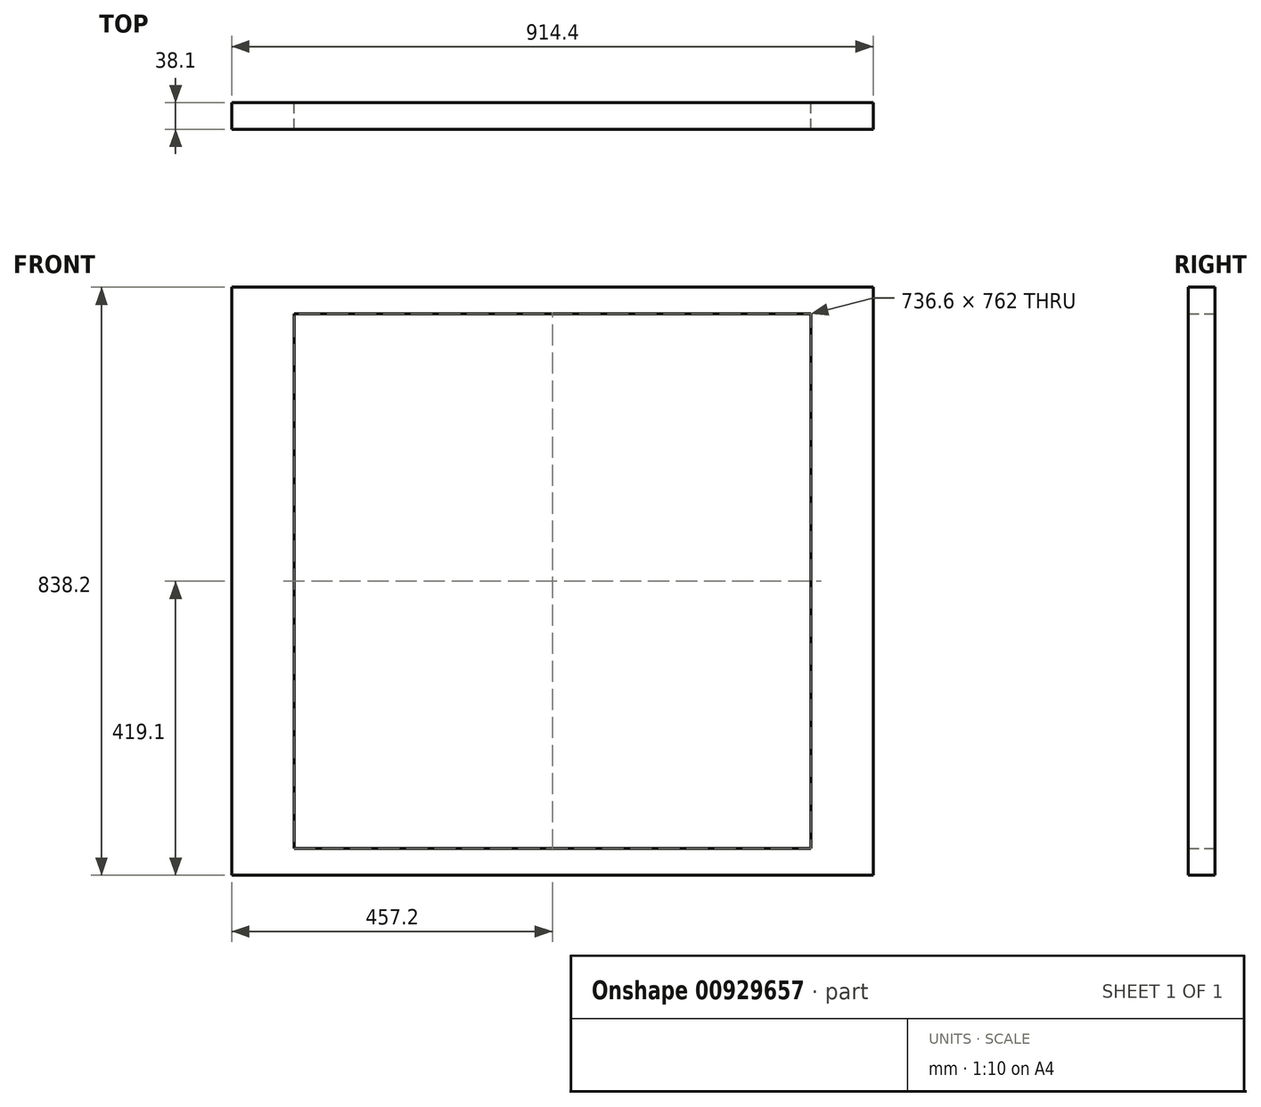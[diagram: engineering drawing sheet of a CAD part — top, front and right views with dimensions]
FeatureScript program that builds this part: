
annotation { "Feature Type Name" : "Feature", "Feature Type Description" : "" }
export const myFeature = defineFeature(function(context is Context, id is Id, definition is map)
    precondition{}
    {
        {
            var Q0;
            Q0=qCreatedBy(makeId("Front.planeOp"),FACE);
            var sketch = newSketch(context, id + "F0", { "sketchPlane" : qUnion([Q0])});
            skLineSegment(sketch, "E0.bottom", {"start": v(-44.45, -381) * mm, "end": v(44.45, -381) * mm});
            skLineSegment(sketch, "E0.top", {"start": v(-44.45, 381) * mm, "end": v(44.45, 381) * mm});
            skLineSegment(sketch, "E0.left", {"start": v(-44.45, -381) * mm, "end": v(-44.45, 381) * mm});
            skLineSegment(sketch, "E0.right", {"start": v(44.45, -381) * mm, "end": v(44.45, 381) * mm});
            skPoint(sketch, "E0.middle", {"position": v(0, 0) * mm});
            skSolve(sketch);
        }
        {
            var Q0;
            Q0 = qSketchRegion(id + "F0", true);
            extrude(context, id + "F1", {"entities" : qUnion([Q0]), "depth" : 38.1 * mm, "offsetDistance" : 25.4 * mm});
        }
        {
            var Q0;
            Q0=qCreatedBy(makeId("Front.planeOp"),FACE);
            var sketch = newSketch(context, id + "F2", { "sketchPlane" : qUnion([Q0])});
            skLineSegment(sketch, "E1.bottom", {"start": v(-44.45, 381) * mm, "end": v(869.95, 381) * mm});
            skLineSegment(sketch, "E1.top", {"start": v(-44.45, 419.1) * mm, "end": v(869.95, 419.1) * mm});
            skLineSegment(sketch, "E1.left", {"start": v(-44.45, 381) * mm, "end": v(-44.45, 419.1) * mm});
            skLineSegment(sketch, "E1.right", {"start": v(869.95, 381) * mm, "end": v(869.95, 419.1) * mm});
            skSolve(sketch);
        }
        {
            var Q0;
            Q0=makeQuery(id+"F2.imprint","IMPRINT",FACE,{"disambiguationData":[TD([[makeQuery(id+"F2.imprint","IMPRINT",EDGE,{"derivedFrom":sQuery(id+"F2.wireOp",EDGE,"E1.bottom")}),1.0]])]});
            extrude(context, id + "F3", {"entities" : qUnion([Q0]), "operationType" : NewBodyOperationType.ADD, "depth" : 38.1 * mm, "offsetDistance" : 25.4 * mm});
        }
        {
            var Q0;
            Q0=qCreatedBy(makeId("Front.planeOp"),FACE);
            var sketch = newSketch(context, id + "F4", { "sketchPlane" : qUnion([Q0])});
            skLineSegment(sketch, "E2.bottom", {"start": v(781.05, -381) * mm, "end": v(869.95, -381) * mm});
            skLineSegment(sketch, "E2.top", {"start": v(781.05, 381) * mm, "end": v(869.95, 381) * mm});
            skLineSegment(sketch, "E2.left", {"start": v(781.05, -381) * mm, "end": v(781.05, 381) * mm});
            skLineSegment(sketch, "E2.right", {"start": v(869.95, -381) * mm, "end": v(869.95, 381) * mm});
            skPoint(sketch, "E2.middle", {"position": v(825.5, 0) * mm});
            skSolve(sketch);
        }
        {
            var Q0;
            Q0=makeQuery(id+"F4.imprint","IMPRINT",FACE,{"disambiguationData":[TD([[makeQuery(id+"F4.imprint","IMPRINT",EDGE,{"derivedFrom":sQuery(id+"F4.wireOp",EDGE,"E2.bottom")}),1.0]])]});
            extrude(context, id + "F5", {"entities" : qUnion([Q0]), "operationType" : NewBodyOperationType.ADD, "depth" : 38.1 * mm, "offsetDistance" : 25.4 * mm});
        }
        {
            var Q0;
            Q0=qCreatedBy(makeId("Front.planeOp"),FACE);
            var sketch = newSketch(context, id + "F6", { "sketchPlane" : qUnion([Q0])});
            skLineSegment(sketch, "E3.bottom", {"start": v(-44.45, -419.1) * mm, "end": v(869.95, -419.1) * mm});
            skLineSegment(sketch, "E3.top", {"start": v(-44.45, -381) * mm, "end": v(869.95, -381) * mm});
            skLineSegment(sketch, "E3.left", {"start": v(-44.45, -419.1) * mm, "end": v(-44.45, -381) * mm});
            skLineSegment(sketch, "E3.right", {"start": v(869.95, -419.1) * mm, "end": v(869.95, -381) * mm});
            skSolve(sketch);
        }
        {
            var Q0;
            Q0=makeQuery(id+"F6.imprint","IMPRINT",FACE,{"disambiguationData":[TD([[makeQuery(id+"F6.imprint","IMPRINT",EDGE,{"derivedFrom":sQuery(id+"F6.wireOp",EDGE,"E3.bottom")}),1.0]])]});
            extrude(context, id + "F7", {"entities" : qUnion([Q0]), "operationType" : NewBodyOperationType.ADD, "depth" : 38.1 * mm, "offsetDistance" : 25.4 * mm});
        }
    });
